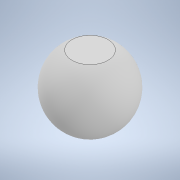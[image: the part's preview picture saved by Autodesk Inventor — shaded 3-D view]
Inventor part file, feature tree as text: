
AUTODESK INVENTOR PART (.ipt)
format: ipt  version: 2022 (Build 260153000, 153)  size: 122,880 bytes
history: native  units: mm
features: revolve x1, sketch x1
ambient origin geometry x8: Origin, YZ Plane, XZ Plane, XY Plane, X Axis, Y Axis, Z Axis, Center Point
bodies: Solid1 (feature_tree)
feature tree (2):
  revolve  "Revolution1"  [1 undecoded]
  sketch  "Sketch1"  dims[d0=10.0mm d1=9.37mm d2=90.0deg]
note: 1 required parameter value undecoded (feature->parameter linkage not recoverable at this tier; creation-order binding heuristic only, values carry confidence <= 0.55)
